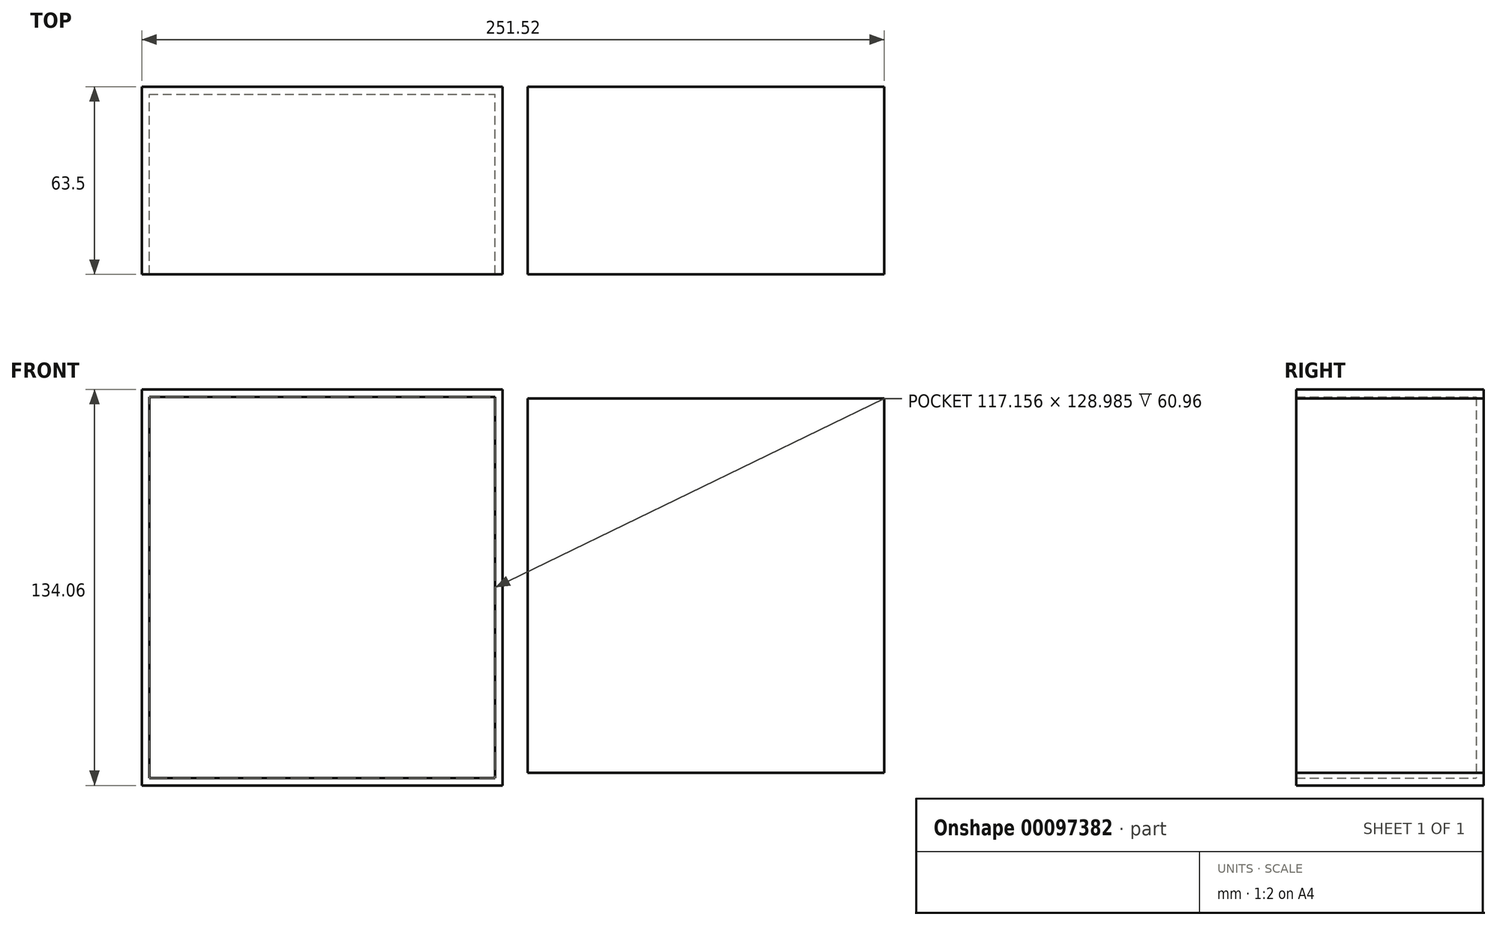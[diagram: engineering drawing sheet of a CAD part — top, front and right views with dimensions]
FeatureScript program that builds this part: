
annotation { "Feature Type Name" : "Feature", "Feature Type Description" : "" }
export const myFeature = defineFeature(function(context is Context, id is Id, definition is map)
    precondition{}
    {
        {
            var Q0;
            Q0=qCreatedBy(makeId("Front.planeOp"),FACE);
            var sketch = newSketch(context, id + "F0", { "sketchPlane" : qUnion([Q0])});
            skLineSegment(sketch, "E0.bottom", {"start": v(-60.82, 67.65) * mm, "end": v(61.42, 67.65) * mm});
            skLineSegment(sketch, "E0.top", {"start": v(-60.82, -66.41) * mm, "end": v(61.42, -66.41) * mm});
            skLineSegment(sketch, "E0.left", {"start": v(-60.82, 67.65) * mm, "end": v(-60.82, -66.41) * mm});
            skLineSegment(sketch, "E0.right", {"start": v(61.42, 67.65) * mm, "end": v(61.42, -66.41) * mm});
            skSolve(sketch);
        }
        {
            var Q0;
            Q0=makeQuery(id+"F0.imprint","IMPRINT",FACE,{"disambiguationData":[TD([[makeQuery(id+"F0.imprint","IMPRINT",EDGE,{"derivedFrom":sQuery(id+"F0.wireOp",EDGE,"E0.bottom")}),-1.0]])]});
            extrude(context, id + "F5", {"entities" : qUnion([Q0]), "depth" : 63.5 * mm});
        }
        {
            var Q0;
            Q0=makeQuery(id+"F5.opExtrude","CAP_FACE",FACE,{"disambiguationData":[OSD([sQuery(id+"F0.wireOp",EDGE,"E0.bottom"),sQuery(id+"F0.wireOp",EDGE,"E0.top"),sQuery(id+"F0.wireOp",EDGE,"E0.left"),sQuery(id+"F0.wireOp",EDGE,"E0.right")])],"isStart":false});
            shell(context, id + "F6", {"entities" : qUnion([Q0]), "thickness" : 2.54 * mm});
        }
        {
            var Q0;
            Q0=qCreatedBy(makeId("Front.planeOp"),FACE);
            var sketch = newSketch(context, id + "F1", { "sketchPlane" : qUnion([Q0])});
            skLineSegment(sketch, "E1.bottom", {"start": v(69.93, 64.61) * mm, "end": v(190.7, 64.61) * mm});
            skLineSegment(sketch, "E1.top", {"start": v(69.93, -62.1) * mm, "end": v(190.7, -62.1) * mm});
            skLineSegment(sketch, "E1.left", {"start": v(69.93, 64.61) * mm, "end": v(69.93, -62.1) * mm});
            skLineSegment(sketch, "E1.right", {"start": v(190.7, 64.61) * mm, "end": v(190.7, -62.1) * mm});
            skSolve(sketch);
        }
        {
            var Q0;
            Q0=makeQuery(id+"F1.imprint","IMPRINT",FACE,{"disambiguationData":[TD([[makeQuery(id+"F1.imprint","IMPRINT",EDGE,{"derivedFrom":sQuery(id+"F1.wireOp",EDGE,"E1.bottom")}),-1.0]])]});
            extrude(context, id + "F2", {"entities" : qUnion([Q0]), "depth" : 63.5 * mm});
        }
        {
            var Q0;
            Q0=makeQuery(id+"F2.opExtrude","SWEPT_FACE",FACE,{"disambiguationData":[OSD([sQuery(id+"F1.wireOp",EDGE,"E1.right")])]});
            var sketch = newSketch(context, id + "F3", { "sketchPlane" : qUnion([Q0])});
            skCircle(sketch, "E2", {"center": v(-52.44, -99.5) * mm, "radius": 11.06 * mm});
            skSolve(sketch);
        }
        {
            var Q0;
            Q0=sQuery(id+"F3.wireOp",EDGE,"E2");
            extrude(context, id + "F4", {"bodyType" : ToolBodyType.SURFACE, "surfaceEntities" : qUnion([Q0]), "depth" : 63.5 * mm});
        }
    });
